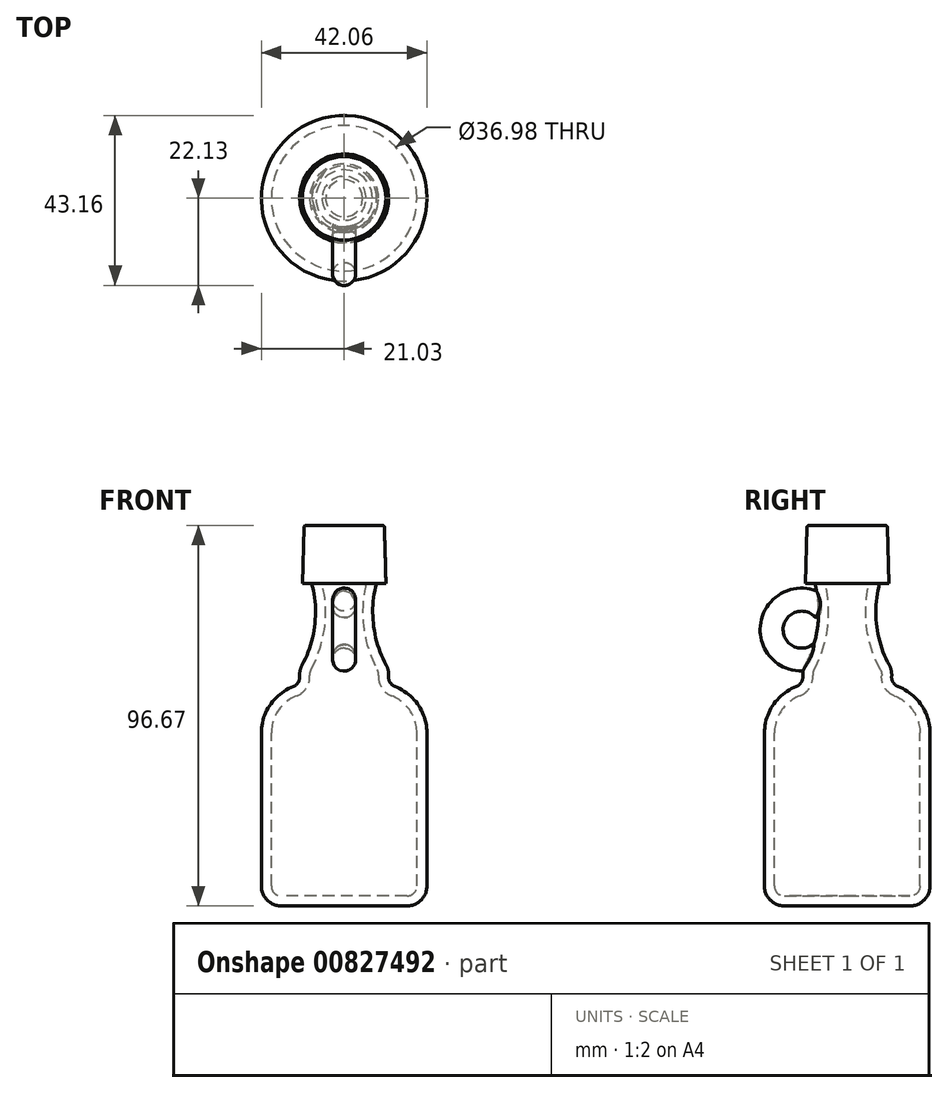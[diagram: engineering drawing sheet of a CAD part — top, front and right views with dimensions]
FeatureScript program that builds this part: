
annotation { "Feature Type Name" : "Feature", "Feature Type Description" : "" }
export const myFeature = defineFeature(function(context is Context, id is Id, definition is map)
    precondition{}
    {
        {
            var Q0;
            Q0=qCreatedBy(makeId("Front.planeOp"),FACE);
            var sketch = newSketch(context, id + "F0", { "sketchPlane" : qUnion([Q0])});
            skLineSegment(sketch, "E0", {"start": v(0, 0) * mm, "end": v(15.95, 0) * mm});
            skLineSegment(sketch, "E1", {"start": v(21.03, 5.08) * mm, "end": v(21.03, 43.93) * mm});
            skArc(sketch, "E2", {"start": v(21.03, 43.93) * mm, "mid": v(18.8, 51.11) * mm, "end": v(12.9, 55.78) * mm});
            skPoint(sketch, "E3.visualSharp", {"position": v(21.03, 0) * mm});
            skArc(sketch, "E3.filletArc", {"start": v(15.95, 0) * mm, "mid": v(19.54, 1.49) * mm, "end": v(21.03, 5.08) * mm});
            skArc(sketch, "E4", {"start": v(8.22, 81.98) * mm, "mid": v(7.46, 71.35) * mm, "end": v(10.7, 61.2) * mm});
            skArc(sketch, "E5", {"start": v(11.3, 58.35) * mm, "mid": v(11.2, 59.82) * mm, "end": v(10.7, 61.2) * mm});
            skPoint(sketch, "E6.visualSharp", {"position": v(10.73, 56.4) * mm});
            skArc(sketch, "E6.filletArc", {"start": v(11.3, 58.35) * mm, "mid": v(11.67, 56.8) * mm, "end": v(12.9, 55.78) * mm});
            skLineSegment(sketch, "E7", {"start": v(0, 81.98) * mm, "end": v(0, 0) * mm});
            skLineSegment(sketch, "E8", {"start": v(0, 81.98) * mm, "end": v(8.22, 81.98) * mm});
            skSolve(sketch);
        }
        {
            var Q0;
            Q0=makeQuery(id+"F0.imprint","IMPRINT",FACE,{"disambiguationData":[TD([[makeQuery(id+"F0.imprint","IMPRINT",EDGE,{"derivedFrom":sQuery(id+"F0.wireOp",EDGE,"E0")}),1.0]])]});
            var Q1;
            Q1=sQuery(id+"F0.wireOp",EDGE,"E4");
            var Q2;
            Q2=sQuery(id+"F0.wireOp",EDGE,"UU5Lz6QZ-6nYC-IxJr-UbMn-F5gGu8TyJ9jb");
            var Q3;
            Q3=sQuery(id+"F0.wireOp",EDGE,"EgvxDOzi-IReg-umcf-xZWc-Wbb1v0iFWshI");
            var Q4;
            Q4=sQuery(id+"F0.wireOp",EDGE,"E5");
            var Q5;
            Q5=sQuery(id+"F0.wireOp",EDGE,"E6.filletArc");
            var Q6;
            Q6=sQuery(id+"F0.wireOp",EDGE,"E2");
            var Q7;
            Q7=sQuery(id+"F0.wireOp",EDGE,"E1");
            var Q8;
            Q8=sQuery(id+"F0.wireOp",EDGE,"E3.filletArc");
            var Q9;
            Q9=sQuery(id+"F0.wireOp",EDGE,"E0");
            var Q10;
            Q10=sQuery(id+"F0.wireOp",EDGE,"1EyvcnN0-Z8o8-A6X2-j4Ha-ReaXHoPqVUWZ");
            var Q11;
            Q11=sQuery(id+"F0.wireOp",EDGE,"a488be62-6a8a-4070-8a87-e226512fef32.filletArc");
            var Q12;
            Q12=sQuery(id+"F0.wireOp",EDGE,"E7");
            revolve(context, id + "F1", {"surfaceOperationType" : NewSurfaceOperationType.NEW, "entities" : qUnion([Q0]), "surfaceEntities" : qUnion([Q1, Q2, Q3, Q4, Q5, Q6, Q7, Q8, Q9, Q10, Q11]), "axis" : qUnion([Q12]), "revolveType" : RevolveType.FULL});
        }
        {
            var Q0;
            Q0=qCreatedBy(makeId("Right.planeOp"),FACE);
            var sketch = newSketch(context, id + "F2", { "sketchPlane" : qUnion([Q0])});
            skArc(sketch, "E9", {"start": v(-6.84, 76.17) * mm, "mid": v(-19.18, 70.9) * mm, "end": v(-7.98, 63.5) * mm});
            skLineSegment(sketch, "E10", {"start": v(-6.84, 76.17) * mm, "end": v(0, 76.17) * mm});
            skLineSegment(sketch, "E11", {"start": v(0, 76.17) * mm, "end": v(0, 63.5) * mm});
            skLineSegment(sketch, "E12", {"start": v(0, 63.5) * mm, "end": v(-7.98, 63.5) * mm});
            skSolve(sketch);
        }
        {
            var Q0;
            Q0=qCreatedBy(makeId("Front.planeOp"),FACE);
            var sketch = newSketch(context, id + "F3", { "sketchPlane" : qUnion([Q0])});
            skCircle(sketch, "E13", {"center": v(0, 76.17) * mm, "radius": 2.92 * mm});
            skSolve(sketch);
        }
        {
            var Q0;
            Q0 = qSketchRegion(id + "F3", true);
            var Q1;
            Q1 = qConstructionFilter(qBodyType(qCreatedBy(id + "F2" ,EDGE), BodyType.WIRE), ConstructionObject.NO);
            sweep(context, id + "F4", {"profiles" : qUnion([Q0]), "path" : qUnion([Q1])});
        }
        {
            var Q0;
            Q0=makeQuery(id+"F1.opRevolve","SWEPT_BODY",BODY,{"disambiguationData":[OSD([sQuery(id+"F0.wireOp",EDGE,"E0"),sQuery(id+"F0.wireOp",EDGE,"E1"),sQuery(id+"F0.wireOp",EDGE,"E2"),sQuery(id+"F0.wireOp",EDGE,"E3.filletArc"),sQuery(id+"F0.wireOp",EDGE,"E4"),sQuery(id+"F0.wireOp",EDGE,"E5"),sQuery(id+"F0.wireOp",EDGE,"E6.filletArc"),sQuery(id+"F0.wireOp",EDGE,"E7"),sQuery(id+"F0.wireOp",EDGE,"E8")])]});
            var Q1;
            Q1=makeQuery(id+"F4.opSweep","SWEPT_BODY",BODY,{"disambiguationData":[OSD([sQuery(id+"F2.wireOp",EDGE,"E10"),sQuery(id+"F3.wireOp",EDGE,"E13")])]});
            booleanBodies(context, id + "F5", {"operationType" : BooleanOperationType.SUBTRACTION, "tools" : qUnion([Q0]), "targets" : qUnion([Q1]), "keepTools" : true});
        }
        {
            var Q0;
            Q0=makeQuery(id+"F1.opRevolve","SWEPT_FACE",FACE,{"disambiguationData":[OSD([sQuery(id+"F0.wireOp",EDGE,"E8")])]});
            shell(context, id + "F6", {"entities" : qUnion([Q0]), "thickness" : 2.54 * mm});
        }
        {
            var Q0;
            Q0=makeQuery(id+"F1.opRevolve","SWEPT_FACE",FACE,{"disambiguationData":[OSD([sQuery(id+"F0.wireOp",EDGE,"E8")])]});
            var sketch = newSketch(context, id + "F7", { "sketchPlane" : qUnion([Q0])});
            skCircle(sketch, "E14", {"center": v(0, 0) * mm, "radius": 10.62 * mm});
            skSolve(sketch);
        }
        {
            var Q0;
            Q0 = qSketchRegion(id + "F7", true);
            var Q1;
            Q1=sQuery(id+"F7.wireOp",EDGE,"E14");
            extrude(context, id + "F8", {"entities" : qUnion([Q0]), "operationType" : NewBodyOperationType.ADD, "surfaceEntities" : qUnion([Q1]), "depth" : 14.68 * mm, "offsetDistance" : 25.4 * mm, "hasDraft" : true, "draftAngle" : 1.5 * degree, "draftPullDirection" : true});
        }
        {
            var Q0;
            Q0=makeQuery(id+"F8.opExtrude","CAP_EDGE",EDGE,{"disambiguationData":[OSD([sQuery(id+"F7.wireOp",EDGE,"E14")])],"isStart":false});
            fillet(context, id + "F9", {"entities" : qUnion([Q0]), "radius" : 0.5 * mm, "tangentPropagation" : true, "allowEdgeOverflow" : false});
        }
        {
            var Q0;
            Q0=makeQuery(id+"F5.opBoolean","INTERSECT",EDGE,{"derivedFrom":[makeQuery(id+"F1.opRevolve","SWEPT_FACE",FACE,{"disambiguationData":[OSD([sQuery(id+"F0.wireOp",EDGE,"E4")])]}),makeQuery(id+"F4.opSweep","SWEPT_FACE",FACE,{"disambiguationData":[OSD([sQuery(id+"F2.wireOp",EDGE,"E9"),sQuery(id+"F3.wireOp",EDGE,"E13")]),OD(0.0)]})]});
            var Q1;
            Q1=makeQuery(id+"F5.opBoolean","INTERSECT",EDGE,{"derivedFrom":[makeQuery(id+"F1.opRevolve","SWEPT_FACE",FACE,{"disambiguationData":[OSD([sQuery(id+"F0.wireOp",EDGE,"E4")])]}),makeQuery(id+"F4.opSweep","SWEPT_FACE",FACE,{"disambiguationData":[OSD([sQuery(id+"F2.wireOp",EDGE,"E12"),sQuery(id+"F3.wireOp",EDGE,"E13")])]})]});
            fillet(context, id + "F10", {"entities" : qUnion([Q0, Q1]), "radius" : 0.03 * mm, "tangentPropagation" : true, "allowEdgeOverflow" : false});
        }
    });
